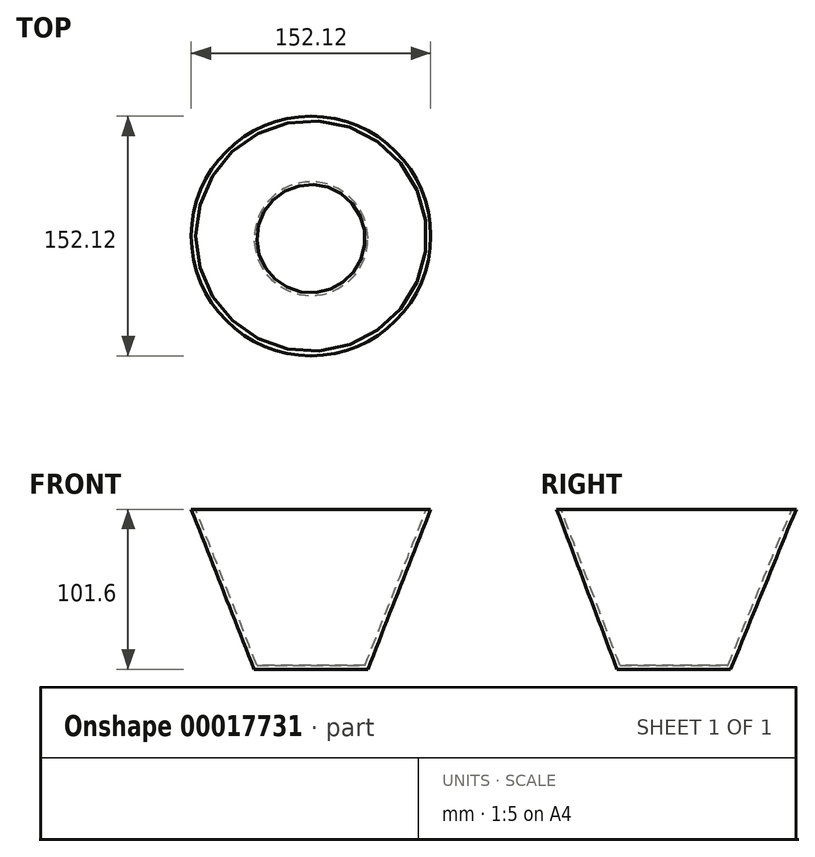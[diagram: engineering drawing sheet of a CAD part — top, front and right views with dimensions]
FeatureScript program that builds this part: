
annotation { "Feature Type Name" : "Feature", "Feature Type Description" : "" }
export const myFeature = defineFeature(function(context is Context, id is Id, definition is map)
    precondition{}
    {
        {
            var Q0;
            Q0=qCreatedBy(makeId("Top.planeOp"),FACE);
            var sketch = newSketch(context, id + "F0", { "sketchPlane" : qUnion([Q0])});
            skCircle(sketch, "E0", {"center": v(0, -1.66) * mm, "radius": 36.1 * mm});
            skSolve(sketch);
        }
        {
            var Q0;
            Q0=qCreatedBy(makeId("Top.planeOp"),FACE);
            cPlane(context, id + "F1", {"entities" : qUnion([Q0]), "cplaneType" : CPlaneType.OFFSET, "offset" : 101.6 * mm, "width" : 152.4 * mm, "height" : 152.4 * mm});
        }
        {
            var Q0;
            Q0=qCreatedBy(id+"F1.planeOp",FACE);
            var sketch = newSketch(context, id + "F2", { "sketchPlane" : qUnion([Q0])});
            skPoint(sketch, "E1.0", {"position": v(0, 0) * mm});
            skCircle(sketch, "E2", {"center": v(0, 0) * mm, "radius": 76.06 * mm});
            skSolve(sketch);
        }
        {
            var Q0;
            Q0=makeQuery(id+"F2.imprint","IMPRINT",FACE,{"disambiguationData":[TD([[makeQuery(id+"F2.imprint","IMPRINT",EDGE,{"derivedFrom":sQuery(id+"F2.wireOp",EDGE,"E2")}),1.0]])]});
            var Q1;
            Q1=makeQuery(id+"F0.imprint","IMPRINT",FACE,{"disambiguationData":[TD([[makeQuery(id+"F0.imprint","IMPRINT",EDGE,{"derivedFrom":sQuery(id+"F0.wireOp",EDGE,"E0")}),1.0]])]});
            loft(context, id + "F3", {"sheetProfilesArray" : [{ "sheetProfileEntities" : qUnion([Q0]) }, { "sheetProfileEntities" : qUnion([Q1]) }]});
        }
        {
            var Q0;
            Q0=makeQuery(id+"F3.opLoft","CAP_FACE",FACE,{"disambiguationData":[OSD([makeQuery(id+"F2.imprint","IMPRINT",FACE,{"disambiguationData":[TD([[makeQuery(id+"F2.imprint","IMPRINT",EDGE,{"derivedFrom":sQuery(id+"F2.wireOp",EDGE,"E2")}),1.0]])]})])],"isStart":true});
            shell(context, id + "F4", {"entities" : qUnion([Q0]), "thickness" : 2.54 * mm});
        }
    });
